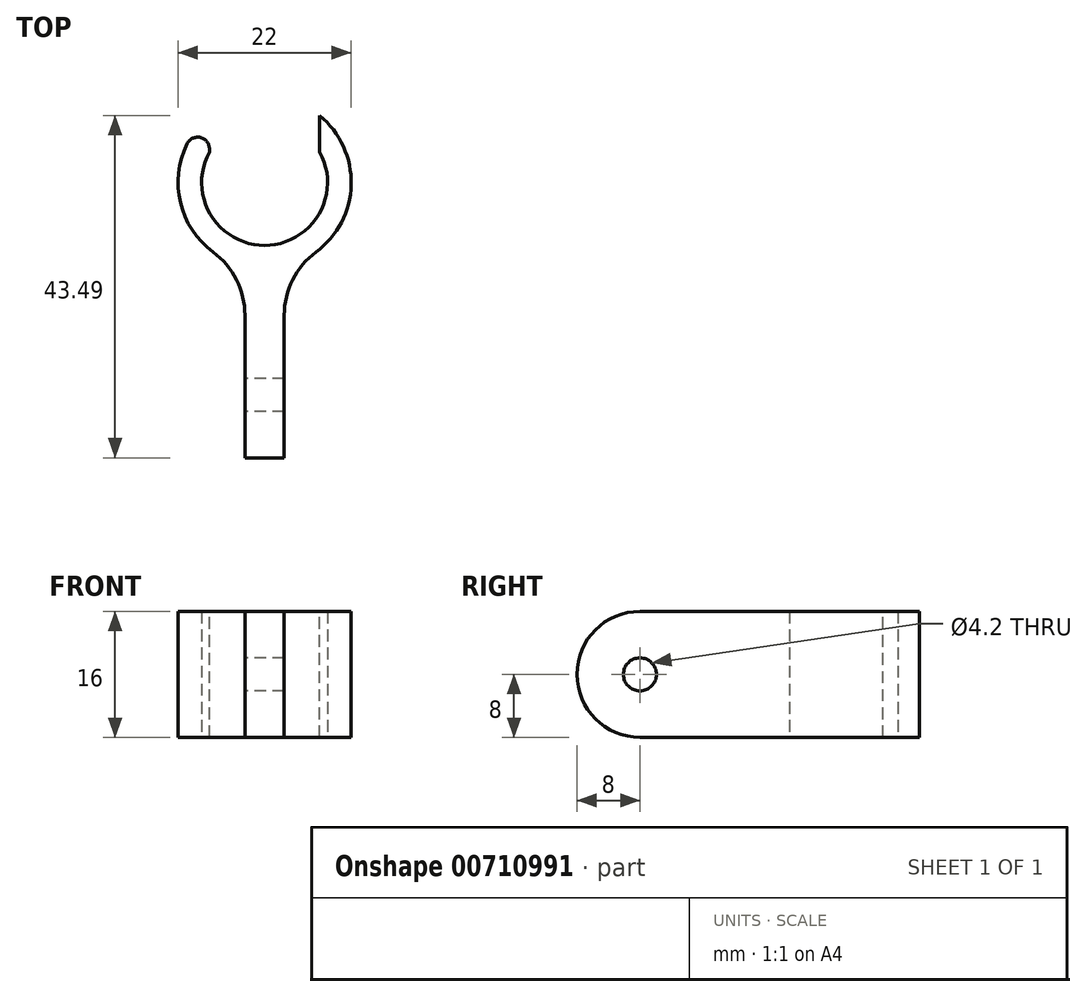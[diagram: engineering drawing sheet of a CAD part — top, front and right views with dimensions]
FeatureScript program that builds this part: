
annotation { "Feature Type Name" : "Feature", "Feature Type Description" : "" }
export const myFeature = defineFeature(function(context is Context, id is Id, definition is map)
    precondition{}
    {
        {
            var Q0;
            Q0=qCreatedBy(makeId("Top.planeOp"),FACE);
            var sketch = newSketch(context, id + "F0", { "sketchPlane" : qUnion([Q0])});
            skCircle(sketch, "E0", {"center": v(0, 0) * mm, "radius": 8 * mm});
            skArc(sketch, "E1", {"start": v(2.5, -10.71) * mm, "mid": v(0, 11) * mm, "end": v(-2.5, -10.71) * mm});
            skLineSegment(sketch, "E2.top", {"start": v(-2.5, -35) * mm, "end": v(2.5, -35) * mm});
            skLineSegment(sketch, "E2.left", {"start": v(-2.5, -10.71) * mm, "end": v(-2.5, -35) * mm});
            skLineSegment(sketch, "E2.right", {"start": v(2.5, -10.71) * mm, "end": v(2.5, -35) * mm});
            skSolve(sketch);
        }
        {
            var Q0;
            Q0=makeQuery(id+"F0.imprint","IMPRINT",FACE,{"disambiguationData":[TD([[makeQuery(id+"F0.imprint","IMPRINT",EDGE,{"derivedFrom":sQuery(id+"F0.wireOp",EDGE,"E0")}),-1.0]])]});
            extrude(context, id + "F1", {"entities" : qUnion([Q0]), "depth" : 16 * mm, "offsetDistance" : 25 * mm});
        }
        {
            var Q0;
            Q0=makeQuery(id+"F1.opExtrude","CAP_FACE",FACE,{"disambiguationData":[OSD([sQuery(id+"F0.wireOp",EDGE,"E0"),sQuery(id+"F0.wireOp",EDGE,"E1")])],"isStart":false});
            var sketch = newSketch(context, id + "F2", { "sketchPlane" : qUnion([Q0])});
            skArc(sketch, "E3.0", {"start": v(7, 3.87) * mm, "mid": v(0, 8) * mm, "end": v(-7, 3.87) * mm});
            skLineSegment(sketch, "E4", {"start": v(-7, 3.87) * mm, "end": v(-7, 8.49) * mm});
            skLineSegment(sketch, "E5", {"start": v(7, 3.87) * mm, "end": v(7, 8.49) * mm});
            skArc(sketch, "E6.0", {"start": v(7, 8.49) * mm, "mid": v(0, 11) * mm, "end": v(-7, 8.49) * mm});
            skPoint(sketch, "E7.orphan", {"position": v(-7, 0) * mm});
            skPoint(sketch, "E8.orphan", {"position": v(7, 0) * mm});
            skSolve(sketch);
        }
        {
            var Q0;
            Q0 = qSketchRegion(id + "F2", true);
            extrude(context, id + "F3", {"entities" : qUnion([Q0]), "operationType" : NewBodyOperationType.REMOVE, "oppositeDirection" : true, "depth" : 25 * mm, "offsetDistance" : 25 * mm});
        }
        {
            var Q0;
            Q0=makeQuery(id+"F3.boolean.opBoolean","COPY",EDGE,{"derivedFrom":makeQuery(id+"F3.opExtrude","SWEPT_EDGE",EDGE,{"disambiguationData":[OSD([sQuery(id+"F0.wireOp",EDGE,"E1"),sQuery(id+"F2.wireOp",EDGE,"E4"),sQuery(id+"F2.wireOp",EDGE,"E6.0")])]})});
            var Q1;
            Q1=makeQuery(id+"F3.boolean.opBoolean","COPY",EDGE,{"derivedFrom":makeQuery(id+"F3.opExtrude","SWEPT_EDGE",EDGE,{"disambiguationData":[OSD([sQuery(id+"F0.wireOp",EDGE,"E1"),sQuery(id+"F2.wireOp",EDGE,"E5"),sQuery(id+"F2.wireOp",EDGE,"E6.0")])]})});
            fillet(context, id + "F4", {"entities" : qUnion([Q0, Q1]), "radius" : 1.5 * mm, "tangentPropagation" : true, "allowEdgeOverflow" : false});
        }
        {
            var Q0;
            Q0=makeQuery(id+"F1.opExtrude","CAP_EDGE",EDGE,{"disambiguationData":[OSD([sQuery(id+"F0.wireOp",EDGE,"E2.top")])],"isStart":false});
            var Q1;
            Q1=makeQuery(id+"F1.opExtrude","CAP_EDGE",EDGE,{"disambiguationData":[OSD([sQuery(id+"F0.wireOp",EDGE,"E2.top")])],"isStart":true});
            fillet(context, id + "F5", {"entities" : qUnion([Q0, Q1]), "radius" : 8 * mm, "tangentPropagation" : true, "allowEdgeOverflow" : false});
        }
        {
            var Q0;
            Q0=makeQuery(id+"F1.opExtrude","SWEPT_EDGE",EDGE,{"disambiguationData":[OSD([sQuery(id+"F0.wireOp",EDGE,"E1"),sQuery(id+"F0.wireOp",EDGE,"E2.left")])]});
            var Q1;
            Q1=makeQuery(id+"F1.opExtrude","SWEPT_EDGE",EDGE,{"disambiguationData":[OSD([sQuery(id+"F0.wireOp",EDGE,"E1"),sQuery(id+"F0.wireOp",EDGE,"E2.right")])]});
            fillet(context, id + "F6", {"entities" : qUnion([Q0, Q1]), "radius" : 10 * mm, "tangentPropagation" : true, "allowEdgeOverflow" : false});
        }
        {
            var Q0;
            Q0=makeQuery(id+"F1.opExtrude","SWEPT_FACE",FACE,{"disambiguationData":[OSD([sQuery(id+"F0.wireOp",EDGE,"E2.left")])]});
            var sketch = newSketch(context, id + "F7", { "sketchPlane" : qUnion([Q0])});
            skArc(sketch, "E9.0", {"start": v(27, 0) * mm, "mid": v(35, 8) * mm, "end": v(27, 16) * mm, "construction": true});
            skCircle(sketch, "E10", {"center": v(27, 8) * mm, "radius": 2.1 * mm});
            skSolve(sketch);
        }
        {
            var Q0;
            Q0 = qSketchRegion(id + "F7", true);
            extrude(context, id + "F8", {"entities" : qUnion([Q0]), "operationType" : NewBodyOperationType.REMOVE, "oppositeDirection" : true, "depth" : 25 * mm, "offsetDistance" : 25 * mm});
        }
    });
